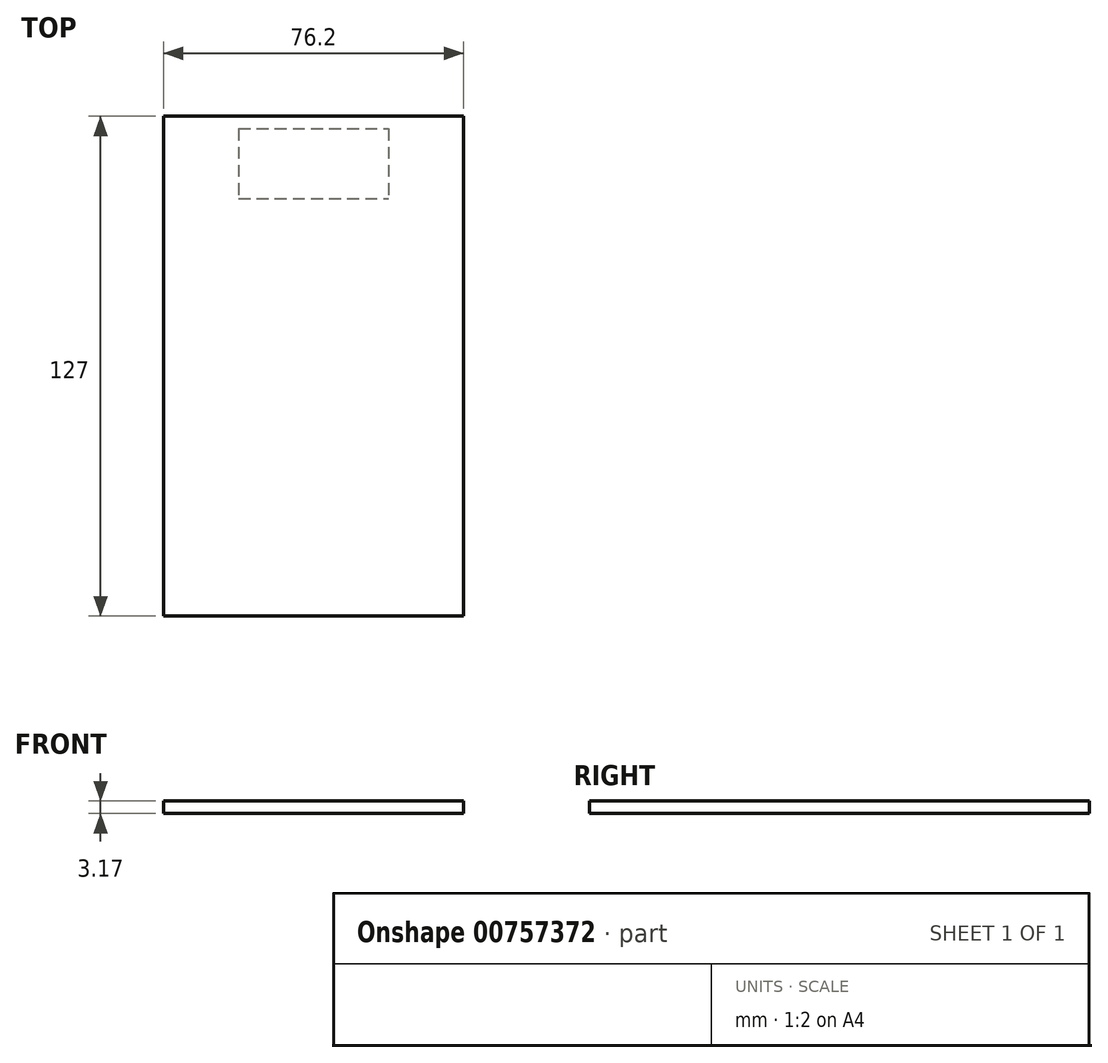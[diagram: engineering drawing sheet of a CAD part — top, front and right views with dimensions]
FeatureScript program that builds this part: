
annotation { "Feature Type Name" : "Feature", "Feature Type Description" : "" }
export const myFeature = defineFeature(function(context is Context, id is Id, definition is map)
    precondition{}
    {
        {
            var Q0;
            Q0=qCreatedBy(makeId("Top.planeOp"),FACE);
            var sketch = newSketch(context, id + "F0", { "sketchPlane" : qUnion([Q0])});
            skLineSegment(sketch, "E0.bottom", {"start": v(-45.54, 74.34) * mm, "end": v(30.66, 74.34) * mm});
            skLineSegment(sketch, "E0.top", {"start": v(-45.54, -52.66) * mm, "end": v(30.66, -52.66) * mm});
            skLineSegment(sketch, "E0.left", {"start": v(-45.54, 74.34) * mm, "end": v(-45.54, -52.66) * mm});
            skLineSegment(sketch, "E0.right", {"start": v(30.66, 74.34) * mm, "end": v(30.66, -52.66) * mm});
            skSolve(sketch);
        }
        {
            var Q0;
            Q0=qSketchRegion(id+"F0",true);
            var Q1;
            Q1=makeQuery(id+"F0.imprint","IMPRINT",FACE,{"disambiguationData":[TD([[makeQuery(id+"F0.imprint","IMPRINT",EDGE,{"derivedFrom":sQuery(id+"F0.wireOp",EDGE,"E0.bottom")}),-1.0]])]});
            extrude(context, id + "F1", {"entities" : qUnion([Q0, Q1]), "depth" : 3.17 * mm, "offsetDistance" : 25.4 * mm});
        }
        {
            var Q0;
            Q0=makeQuery(id+"F1.opExtrude","CAP_FACE",FACE,{"disambiguationData":[OSD([sQuery(id+"F0.wireOp",EDGE,"E0.bottom"),sQuery(id+"F0.wireOp",EDGE,"E0.top"),sQuery(id+"F0.wireOp",EDGE,"E0.left"),sQuery(id+"F0.wireOp",EDGE,"E0.right")])],"isStart":true});
            var sketch = newSketch(context, id + "F2", { "sketchPlane" : qUnion([Q0])});
            skLineSegment(sketch, "E1.right", {"start": v(-26.5, -71.16) * mm, "end": v(-26.5, -53.4) * mm});
            skLineSegment(sketch, "E2.bottom", {"start": v(-26.5, -71.16) * mm, "end": v(11.6, -71.16) * mm});
            skLineSegment(sketch, "E2.top", {"start": v(-26.5, -53.4) * mm, "end": v(11.6, -53.4) * mm});
            skLineSegment(sketch, "E2.right", {"start": v(11.6, -71.16) * mm, "end": v(11.6, -53.4) * mm});
            skSolve(sketch);
        }
        {
            var Q0;
            Q0=qSketchRegion(id+"F2",true);
            extrude(context, id + "F3", {"entities" : qUnion([Q0]), "operationType" : NewBodyOperationType.REMOVE, "oppositeDirection" : true, "depth" : 1 / 203.2 * mm, "offsetDistance" : 25.4 * mm});
        }
    });
